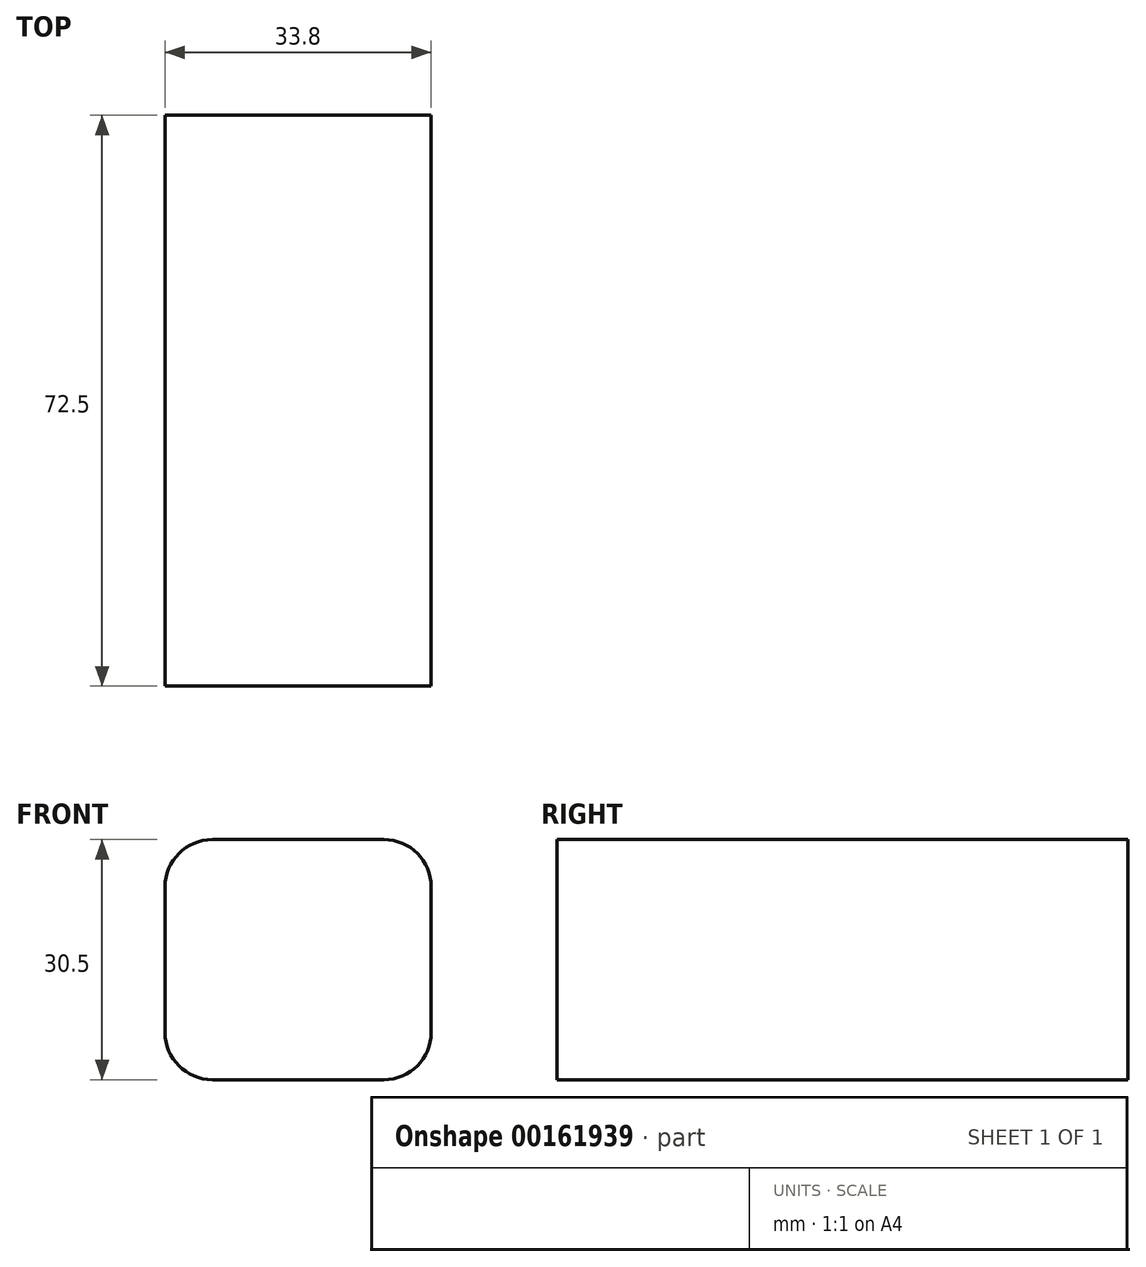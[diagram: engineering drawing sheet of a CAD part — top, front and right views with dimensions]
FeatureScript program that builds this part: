
annotation { "Feature Type Name" : "Feature", "Feature Type Description" : "" }
export const myFeature = defineFeature(function(context is Context, id is Id, definition is map)
    precondition{}
    {
        {
            var Q0;
            Q0=qCreatedBy(makeId("Top.planeOp"),FACE);
            var sketch = newSketch(context, id + "F0", { "sketchPlane" : qUnion([Q0])});
            skLineSegment(sketch, "E0.bottom", {"start": v(16.9, 36.25) * mm, "end": v(-16.9, 36.25) * mm});
            skLineSegment(sketch, "E0.top", {"start": v(16.9, -36.25) * mm, "end": v(-16.9, -36.25) * mm});
            skLineSegment(sketch, "E0.left", {"start": v(16.9, 36.25) * mm, "end": v(16.9, -36.25) * mm});
            skLineSegment(sketch, "E0.right", {"start": v(-16.9, 36.25) * mm, "end": v(-16.9, -36.25) * mm});
            skPoint(sketch, "E0.middle", {"position": v(0, 0) * mm});
            skSolve(sketch);
        }
        {
            var Q0;
            Q0=makeQuery(id+"F0.imprint","IMPRINT",FACE,{"disambiguationData":[TD([[makeQuery(id+"F0.imprint","IMPRINT",EDGE,{"derivedFrom":sQuery(id+"F0.wireOp",EDGE,"E0.bottom")}),1.0]])]});
            extrude(context, id + "F1", {"entities" : qUnion([Q0]), "depth" : 30.5 * mm});
        }
        {
            var Q0;
            Q0=makeQuery(id+"F1.opExtrude","CAP_EDGE",EDGE,{"disambiguationData":[OSD([sQuery(id+"F0.wireOp",EDGE,"E0.left")])],"isStart":false});
            var Q1;
            Q1=makeQuery(id+"F1.opExtrude","CAP_EDGE",EDGE,{"disambiguationData":[OSD([sQuery(id+"F0.wireOp",EDGE,"E0.right")])],"isStart":false});
            var Q2;
            Q2=makeQuery(id+"F1.opExtrude","CAP_EDGE",EDGE,{"disambiguationData":[OSD([sQuery(id+"F0.wireOp",EDGE,"E0.left")])],"isStart":true});
            var Q3;
            Q3=makeQuery(id+"F1.opExtrude","CAP_EDGE",EDGE,{"disambiguationData":[OSD([sQuery(id+"F0.wireOp",EDGE,"E0.right")])],"isStart":true});
            fillet(context, id + "F2", {"entities" : qUnion([Q0, Q1, Q2, Q3]), "radius" : 6 * mm, "tangentPropagation" : true, "allowEdgeOverflow" : false});
        }
    });
